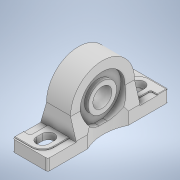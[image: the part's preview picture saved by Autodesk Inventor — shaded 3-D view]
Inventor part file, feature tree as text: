
AUTODESK INVENTOR PART (.ipt)
format: ipt  version: 2020 (Build 240168000, 168)  size: 608,256 bytes
history: native  units: mm
features: extrude x11, sketch x10, projected_geometry x9, other x2, fillet x2
ambient origin geometry x8: Origin, YZ Plane, XZ Plane, XY Plane, X Axis, Y Axis, Z Axis, Center Point
bodies: Body1 (feature_tree)
feature tree (34):
  other  "솔리드1"
  extrude  "돌출1"  Depth=127.0mm
  extrude  "돌출2"  Depth=37.0mm
  fillet  "모깎기1"  Radius=20.0mm
  sketch  "스케치6"
  extrude  "돌출6"  Depth=27.0mm
  other  "작업 평면1"
  extrude  "돌출7"  Depth=42.0mm
  extrude  "돌출8"  Depth=42.0mm
  extrude  "돌출9"  Depth=2.0mm
  extrude  "돌출10"  Depth=13.0mm TaperAngle=0.0deg
  extrude  "돌출11"  Depth=6.0mm
  extrude  "돌출12"  Depth=6.0mm
  extrude  "돌출13"  Depth=6.0mm
  fillet  "모깎기2"  Radius=6.0mm
  extrude  "돌출14"  Depth=6.0mm
  sketch  "스케치1"
  sketch  "스케치2"
  projected_geometry  "투영된 루프1"
  projected_geometry  "투영된 루프4"
  sketch  "스케치10"
  projected_geometry  "투영된 루프6"
  sketch  "스케치11"
  sketch  "스케치12"
  sketch  "스케치13"
  projected_geometry  "투영된 루프7"
  projected_geometry  "투영된 루프8"
  sketch  "스케치14"
  projected_geometry  "투영된 루프9"
  projected_geometry  "투영된 루프10"
  sketch  "스케치15"
  projected_geometry  "투영된 루프11"
  projected_geometry  "투영된 루프12"
  sketch  "스케치16"
